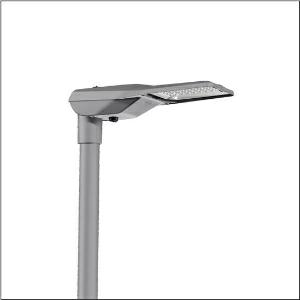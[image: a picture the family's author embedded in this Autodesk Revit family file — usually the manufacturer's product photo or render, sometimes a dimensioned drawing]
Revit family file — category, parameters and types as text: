
# Revit family: streetlight_sl_21_iq_mini___st1_0a_5xe2d31y08gb_99d1
name_source: partatom
category: Lighting Fixtures
units: mm (PartAtom-declared; Revit-internal decimal feet)

## family parameters
Cut with Voids When Loaded = No
Host = Face
Light Source = No
Part Type = Normal
Room Calculation Point = No
Round Connector Dimension = Use Diameter
Shared = No

## types (1)
- --- (1 x LED, 5990 lm, 39.8 W, 3000K)
    Apparent Load = 40 VA
    CIE Flux Codes = 37 72 97 100 100
    Color Rendering = 70
    Color Temperature = 3000K
    Default Elevation = 1800 mm
    Description = Streetlight SL 21 iQ mini, mast luminaire, primary light control with lens, of PMMA, primary optical cover: cover, of toughened safety glass, transparent, light distribution: ST1.0a, light emission: direct distribution, primary light characteristic: asymmetric, installation type: post-top, side-entry, LED, High Power LED, rated luminous flux: 5.990lm, luminous efficacy: 151lm/W, light colour: 730, colour temperature: 3000K, control: presetting dimming logarithmic, Street-Remote, Auto-Match, Temp-Guard, Lumen-Switch, Night-Set, Smart-Wire, Light-Fading, Desk-Remote (wireless, voltage-free reading and setting of iQ features in the workshop via application-optimized NFC function/RFID function), optimised constant luminous flux control (CLO 2.0), mains connection: 220..240V, AC, 50/60Hz, start of lifetime: 40W, end of service life: 41W, reduction: 18W, luminaire housing, of diecast aluminium, powder-coated, Siteco® metallic grey (DB 702S), corrosivity category C5 mid according to DIN EN ISO 12944, please order mast flange separately, inclination adjustable: 0°, 5°, 10°, 15°, sealing non-destructively replaceable, multi-level sealing system, length: 628mm, width: 235mm, height: 110mm, mast flange for spigot size: 42mm (side-entry): 5XC10008XM4, 60/48mm (side-entry/post-top): 5XC10108XM2, 76/60mm (side-entry/post-top): 5XC10108XM1, Smart Interface below and above, protection rating (complete): IP66, insulation class (complete): insulation class II (safety insulation), certification: CE, ENEC, ENEC+, VDE, impact resistance: IK09, permissible operating ambient temperature for outdoor applications: -40..+50°C, standard-compliant lighting for roads and squares, packaging unit: 1 piece

Light Distribution: ST1.0a
    Height = 110 mm
    Lamp = 1 x LED
    Lamp Light Flux = 5990 lm
    Lamp Power = 39.8 W
    Lamp count = 1
    Length = 625 mm
    Luminous efficacy = 151 lm/W
    Manufacturer = Siteco
    ModVariant = No
    Model = 5XE2D31Y08GB
    Number of Poles = 1
    OnlyDefault = Yes
    Power Factor = 1
    Product Name = Streetlight SL 21 iQ mini | ST1.0a
    Product group = mast luminaire | pylon top
    ProductGroupID = 6100
    Protection Class = Protection class II
    Protection Degree = IP 66
    RLX_Detail_Level = 1
    RLX_Emergency_Light_Flux = 0 lm
    RLX_Emergency_Type = 0
    RLX_Emergency_Type_DB = No
    RlxData = <blob elided: 92497 chars, md5=3cfa8e7a>
    Socket = socket
    Standby Power = 0 W
    System Light Flux = 5990 lm
    System Power = 40 W
    Type Comments = factory setting: luminous flux: 100 % | dim-lin: 254 | 800 mA
    Type Image = l_1003514.jpg
    URL = http://relux.com
    VarID = @adj_063111
    Voltage = 0 V
    Weight = 0.00 kg
    Width = 234 mm

## geometry (parser evidence)
native form markers: Blend x4, Sweep x10
no freeform markers — native parametric forms only
